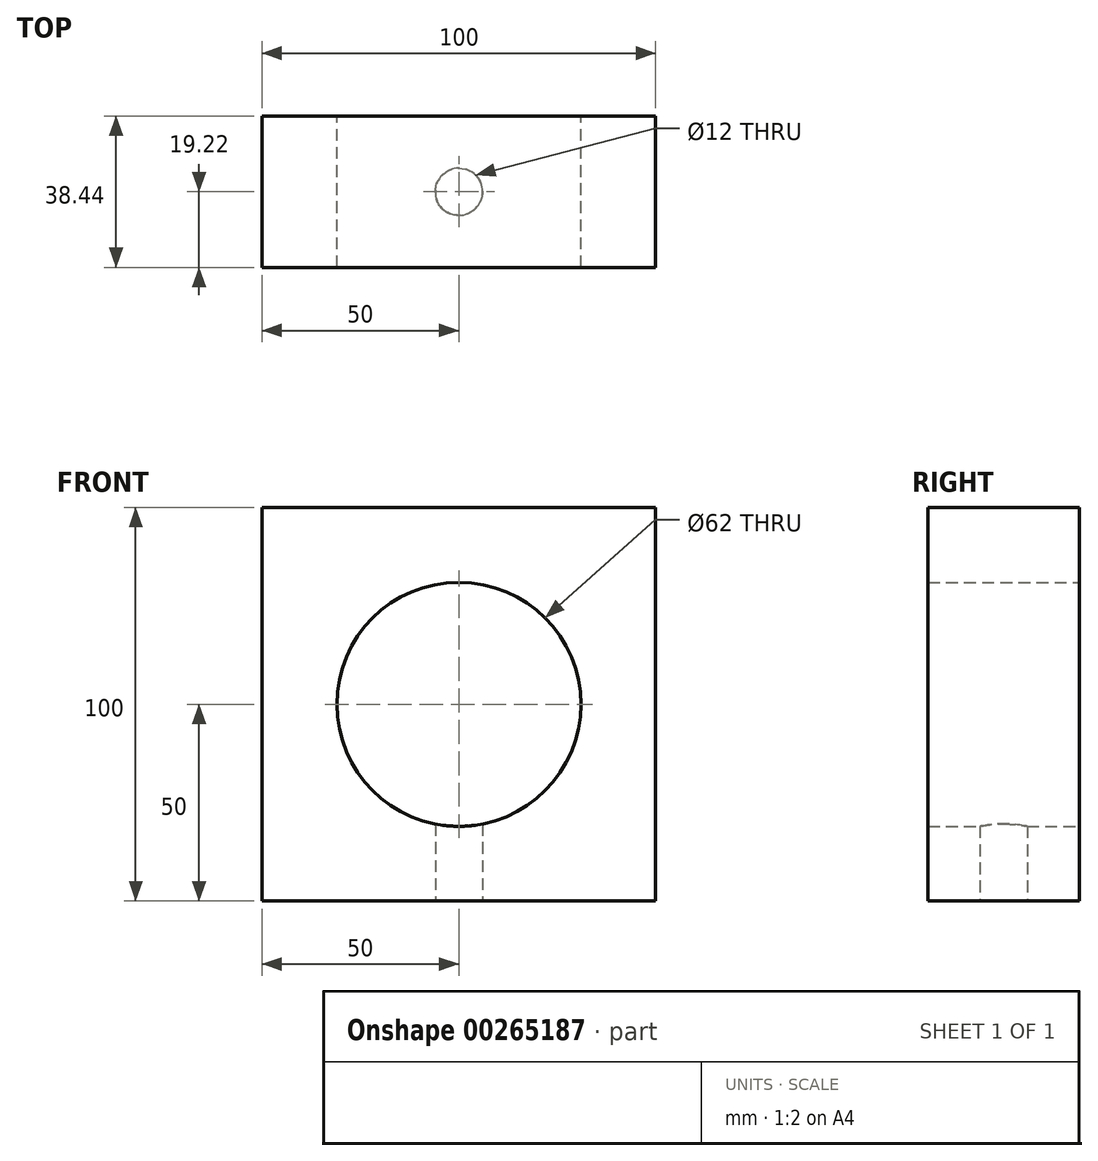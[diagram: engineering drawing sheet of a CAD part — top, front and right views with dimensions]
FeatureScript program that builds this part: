
annotation { "Feature Type Name" : "Feature", "Feature Type Description" : "" }
export const myFeature = defineFeature(function(context is Context, id is Id, definition is map)
    precondition{}
    {
        {
            var Q0;
            Q0=qCreatedBy(makeId("Front.planeOp"),FACE);
            var sketch = newSketch(context, id + "F0", { "sketchPlane" : qUnion([Q0])});
            skCircle(sketch, "E0", {"center": v(0, 0) * mm, "radius": 31 * mm});
            skLineSegment(sketch, "E1.bottom", {"start": v(50, 50) * mm, "end": v(-50, 50) * mm});
            skLineSegment(sketch, "E1.top", {"start": v(50, -50) * mm, "end": v(-50, -50) * mm});
            skLineSegment(sketch, "E1.left", {"start": v(50, 50) * mm, "end": v(50, -50) * mm});
            skLineSegment(sketch, "E1.right", {"start": v(-50, 50) * mm, "end": v(-50, -50) * mm});
            skSolve(sketch);
        }
        {
            var Q0;
            Q0 = qSketchRegion(id + "F0", true);
            extrude(context, id + "F1", {"entities" : qUnion([Q0]), "depth" : (62 * 0.62) * mm});
        }
        {
            var Q0;
            Q0=makeQuery(id+"F1.opExtrude","SWEPT_FACE",FACE,{"disambiguationData":[OSD([sQuery(id+"F0.wireOp",EDGE,"E1.top")])]});
            var sketch = newSketch(context, id + "F2", { "sketchPlane" : qUnion([Q0])});
            skLineSegment(sketch, "E2", {"start": v(0, 38.44) * mm, "end": v(0, 0) * mm, "construction": true});
            skCircle(sketch, "E3", {"center": v(0, 19.22) * mm, "radius": 6 * mm});
            skSolve(sketch);
        }
        {
            var Q0;
            Q0 = qSketchRegion(id + "F2", true);
            extrude(context, id + "F3", {"entities" : qUnion([Q0]), "operationType" : NewBodyOperationType.REMOVE, "endBound" : BoundingType.UP_TO_NEXT, "oppositeDirection" : true, "depth" : 25 * mm});
        }
    });
